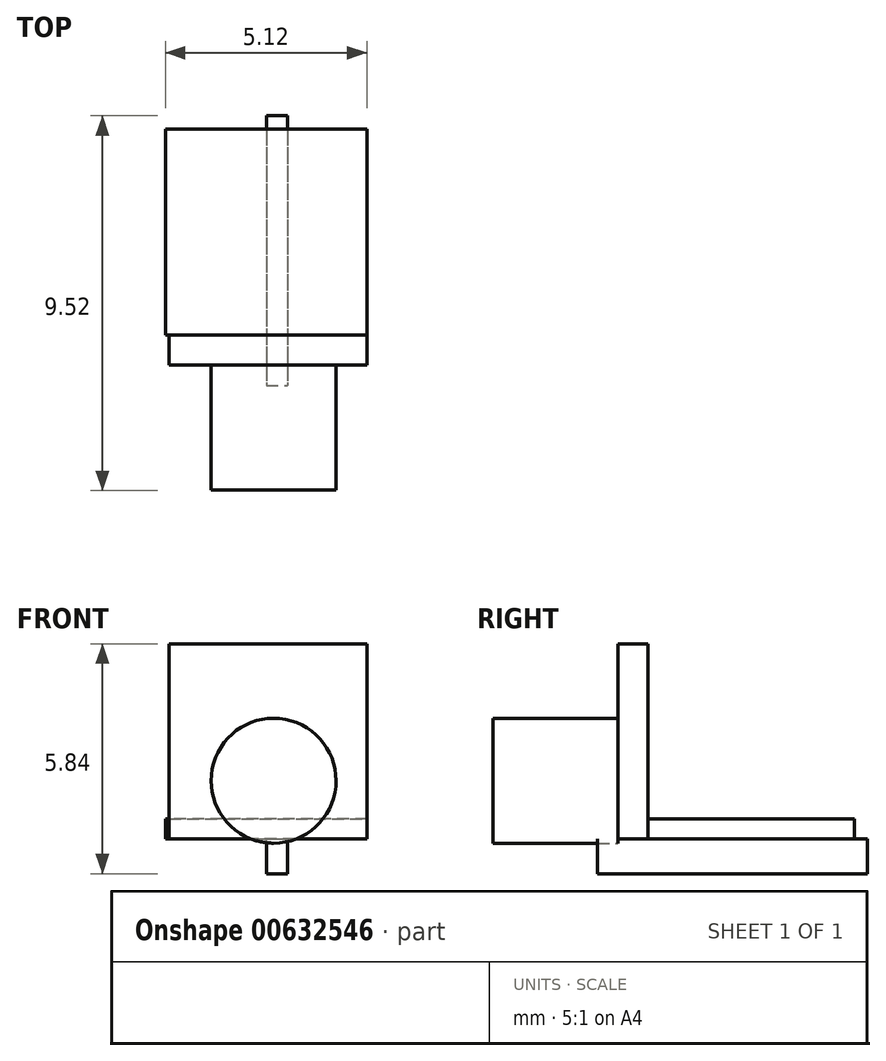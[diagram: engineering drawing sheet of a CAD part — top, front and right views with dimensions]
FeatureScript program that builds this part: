
annotation { "Feature Type Name" : "Feature", "Feature Type Description" : "" }
export const myFeature = defineFeature(function(context is Context, id is Id, definition is map)
    precondition{}
    {
        {
            var Q0;
            Q0=qCreatedBy(makeId("Front.planeOp"),FACE);
            var sketch = newSketch(context, id + "F0", { "sketchPlane" : qUnion([Q0])});
            skCircle(sketch, "E0", {"center": v(-24.2, 23.9) * mm, "radius": 1.59 * mm});
            skSolve(sketch);
        }
        {
            var Q0;
            Q0=makeQuery(id+"F0.imprint","IMPRINT",FACE,{"disambiguationData":[TD([[makeQuery(id+"F0.imprint","IMPRINT",EDGE,{"derivedFrom":sQuery(id+"F0.wireOp",EDGE,"E0")}),1.0]])]});
            extrude(context, id + "F1", {"entities" : qUnion([Q0]), "depth" : 3.17 * mm, "offsetDistance" : 25.4 * mm});
        }
        {
            var Q0;
            Q0=qCreatedBy(makeId("Front.planeOp"),FACE);
            var sketch = newSketch(context, id + "F2", { "sketchPlane" : qUnion([Q0])});
            skLineSegment(sketch, "E1.bottom", {"start": v(-26.86, 22.42) * mm, "end": v(-21.83, 22.42) * mm});
            skLineSegment(sketch, "E1.top", {"start": v(-26.86, 27.37) * mm, "end": v(-21.83, 27.37) * mm});
            skLineSegment(sketch, "E1.left", {"start": v(-26.86, 22.42) * mm, "end": v(-26.86, 27.37) * mm});
            skLineSegment(sketch, "E1.right", {"start": v(-21.83, 22.42) * mm, "end": v(-21.83, 27.37) * mm});
            skSolve(sketch);
        }
        {
            var Q0;
            Q0=makeQuery(id+"F2.imprint","IMPRINT",FACE,{"disambiguationData":[TD([[makeQuery(id+"F2.imprint","IMPRINT",EDGE,{"derivedFrom":sQuery(id+"F2.wireOp",EDGE,"E1.bottom")}),1.0]])]});
            extrude(context, id + "F3", {"entities" : qUnion([Q0]), "operationType" : NewBodyOperationType.ADD, "oppositeDirection" : true, "depth" : 0.76 * mm, "offsetDistance" : 25.4 * mm});
        }
        {
            var Q0;
            Q0=makeQuery(id+"F3.opExtrude","SWEPT_FACE",FACE,{"disambiguationData":[OSD([sQuery(id+"F2.wireOp",EDGE,"E1.bottom")])]});
            var sketch = newSketch(context, id + "F4", { "sketchPlane" : qUnion([Q0])});
            skLineSegment(sketch, "E2.bottom", {"start": v(-21.83, -0.76) * mm, "end": v(-26.95, -0.76) * mm});
            skLineSegment(sketch, "E2.top", {"start": v(-21.83, -6) * mm, "end": v(-26.95, -6) * mm});
            skLineSegment(sketch, "E2.left", {"start": v(-21.83, -0.76) * mm, "end": v(-21.83, -6) * mm});
            skLineSegment(sketch, "E2.right", {"start": v(-26.95, -0.76) * mm, "end": v(-26.95, -6) * mm});
            skSolve(sketch);
        }
        {
            var Q0;
            Q0 = qSketchRegion(id + "F4", true);
            extrude(context, id + "F5", {"entities" : qUnion([Q0]), "oppositeDirection" : true, "depth" : 0.5 * mm, "offsetDistance" : 25.4 * mm});
        }
        {
            var Q0;
            Q0=makeQuery(id+"F3.opExtrude","SWEPT_FACE",FACE,{"disambiguationData":[OSD([sQuery(id+"F2.wireOp",EDGE,"E1.bottom")])]});
            var sketch = newSketch(context, id + "F6", { "sketchPlane" : qUnion([Q0])});
            skLineSegment(sketch, "E3.bottom", {"start": v(-24.39, -6.34) * mm, "end": v(-23.85, -6.34) * mm});
            skLineSegment(sketch, "E3.top", {"start": v(-24.39, 0.52) * mm, "end": v(-23.85, 0.52) * mm});
            skLineSegment(sketch, "E3.left", {"start": v(-24.39, -6.34) * mm, "end": v(-24.39, 0.52) * mm});
            skLineSegment(sketch, "E3.right", {"start": v(-23.85, -6.34) * mm, "end": v(-23.85, 0.52) * mm});
            skSolve(sketch);
        }
        {
            var Q0;
            Q0 = qSketchRegion(id + "F6", true);
            extrude(context, id + "F7", {"entities" : qUnion([Q0]), "depth" : 0.89 * mm, "offsetDistance" : 25.4 * mm});
        }
    });
